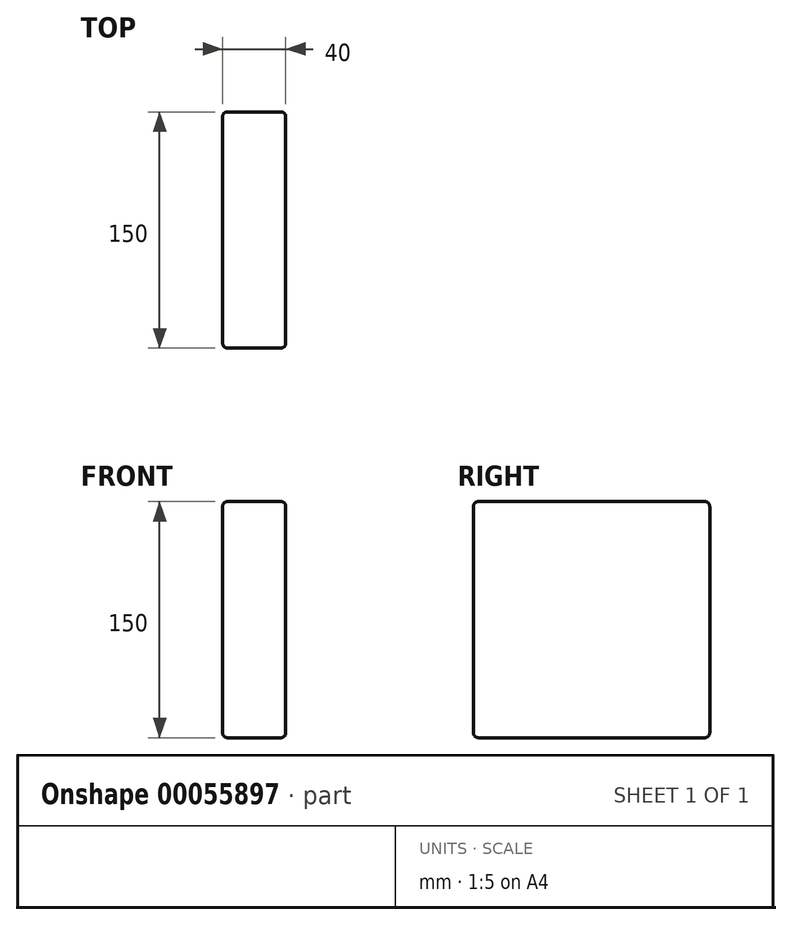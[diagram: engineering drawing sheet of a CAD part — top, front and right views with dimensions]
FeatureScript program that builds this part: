
annotation { "Feature Type Name" : "Feature", "Feature Type Description" : "" }
export const myFeature = defineFeature(function(context is Context, id is Id, definition is map)
    precondition{}
    {
        {
            var Q0;
            Q0=qCreatedBy(makeId("Right.planeOp"),FACE);
            var sketch = newSketch(context, id + "F0", { "sketchPlane" : qUnion([Q0])});
            skLineSegment(sketch, "E0.bottom", {"start": v(-70.5, 82.62) * mm, "end": v(79.5, 82.62) * mm});
            skLineSegment(sketch, "E0.top", {"start": v(-70.5, -67.38) * mm, "end": v(79.5, -67.38) * mm});
            skLineSegment(sketch, "E0.left", {"start": v(-70.5, 82.62) * mm, "end": v(-70.5, -67.38) * mm});
            skLineSegment(sketch, "E0.right", {"start": v(79.5, 82.62) * mm, "end": v(79.5, -67.38) * mm});
            skSolve(sketch);
        }
        {
            var Q0;
            Q0 = qSketchRegion(id + "F0", true);
            extrude(context, id + "F1", {"entities" : qUnion([Q0]), "depth" : 40 * mm});
        }
        {
            var Q0;
            Q0=makeQuery(id+"F1.opExtrude","SWEPT_EDGE",EDGE,{"disambiguationData":[OSD([sQuery(id+"F0.wireOp",EDGE,"E0.bottom"),sQuery(id+"F0.wireOp",EDGE,"E0.left")])]});
            var Q1;
            Q1=makeQuery(id+"F1.opExtrude","CAP_EDGE",EDGE,{"disambiguationData":[OSD([sQuery(id+"F0.wireOp",EDGE,"E0.bottom")])],"isStart":false});
            var Q2;
            Q2=makeQuery(id+"F1.opExtrude","CAP_EDGE",EDGE,{"disambiguationData":[OSD([sQuery(id+"F0.wireOp",EDGE,"E0.bottom")])],"isStart":true});
            var Q3;
            Q3=makeQuery(id+"F1.opExtrude","SWEPT_EDGE",EDGE,{"disambiguationData":[OSD([sQuery(id+"F0.wireOp",EDGE,"E0.bottom"),sQuery(id+"F0.wireOp",EDGE,"E0.right")])]});
            var Q4;
            Q4=makeQuery(id+"F1.opExtrude","CAP_EDGE",EDGE,{"disambiguationData":[OSD([sQuery(id+"F0.wireOp",EDGE,"E0.left")])],"isStart":false});
            var Q5;
            Q5=makeQuery(id+"F1.opExtrude","CAP_EDGE",EDGE,{"disambiguationData":[OSD([sQuery(id+"F0.wireOp",EDGE,"E0.left")])],"isStart":true});
            var Q6;
            Q6=makeQuery(id+"F1.opExtrude","CAP_EDGE",EDGE,{"disambiguationData":[OSD([sQuery(id+"F0.wireOp",EDGE,"E0.top")])],"isStart":false});
            var Q7;
            Q7=makeQuery(id+"F1.opExtrude","SWEPT_EDGE",EDGE,{"disambiguationData":[OSD([sQuery(id+"F0.wireOp",EDGE,"E0.top"),sQuery(id+"F0.wireOp",EDGE,"E0.left")])]});
            var Q8;
            Q8=makeQuery(id+"F1.opExtrude","CAP_EDGE",EDGE,{"disambiguationData":[OSD([sQuery(id+"F0.wireOp",EDGE,"E0.right")])],"isStart":false});
            var Q9;
            Q9=makeQuery(id+"F1.opExtrude","CAP_EDGE",EDGE,{"disambiguationData":[OSD([sQuery(id+"F0.wireOp",EDGE,"E0.right")])],"isStart":true});
            var Q10;
            Q10=makeQuery(id+"F1.opExtrude","SWEPT_EDGE",EDGE,{"disambiguationData":[OSD([sQuery(id+"F0.wireOp",EDGE,"E0.top"),sQuery(id+"F0.wireOp",EDGE,"E0.right")])]});
            var Q11;
            Q11=makeQuery(id+"F1.opExtrude","CAP_EDGE",EDGE,{"disambiguationData":[OSD([sQuery(id+"F0.wireOp",EDGE,"E0.top")])],"isStart":true});
            fillet(context, id + "F2", {"entities" : qUnion([Q0, Q1, Q2, Q3, Q4, Q5, Q6, Q7, Q8, Q9, Q10, Q11]), "radius" : 3 * mm, "tangentPropagation" : true, "allowEdgeOverflow" : false});
        }
    });
